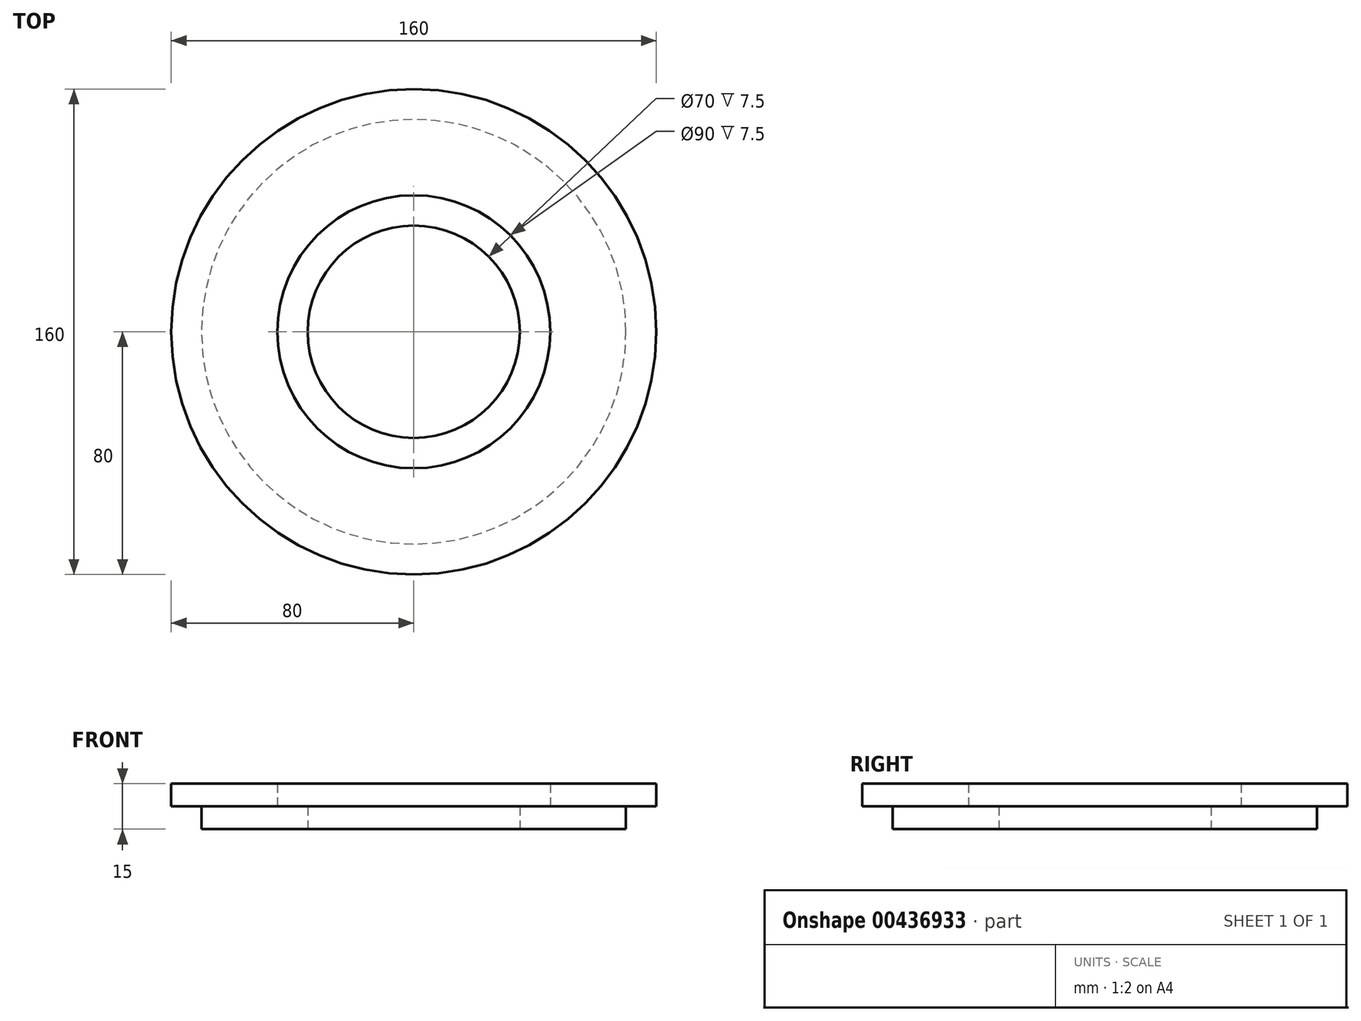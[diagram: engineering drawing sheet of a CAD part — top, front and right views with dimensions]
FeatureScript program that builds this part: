
annotation { "Feature Type Name" : "Feature", "Feature Type Description" : "" }
export const myFeature = defineFeature(function(context is Context, id is Id, definition is map)
    precondition{}
    {
        {
            var Q0;
            Q0=qCreatedBy(makeId("Front.planeOp"),FACE);
            var sketch = newSketch(context, id + "F0", { "sketchPlane" : qUnion([Q0])});
            skLineSegment(sketch, "E0", {"start": v(35, 0) * mm, "end": v(70, 0) * mm});
            skLineSegment(sketch, "E1", {"start": v(70, 0) * mm, "end": v(70, 7.5) * mm});
            skLineSegment(sketch, "E2", {"start": v(70, 7.5) * mm, "end": v(80, 7.5) * mm});
            skLineSegment(sketch, "E3", {"start": v(80, 7.5) * mm, "end": v(80, 15) * mm});
            skLineSegment(sketch, "E4", {"start": v(80, 15) * mm, "end": v(45, 15) * mm});
            skLineSegment(sketch, "E5", {"start": v(45, 15) * mm, "end": v(45, 7.5) * mm});
            skLineSegment(sketch, "E6", {"start": v(45, 7.5) * mm, "end": v(35, 7.5) * mm});
            skLineSegment(sketch, "E7", {"start": v(35, 7.5) * mm, "end": v(35, 0) * mm});
            skLineSegment(sketch, "E8", {"start": v(0, 0) * mm, "end": v(0, 115.63) * mm, "construction": true});
            skSolve(sketch);
        }
        {
            var Q0;
            Q0=makeQuery(id+"F0.imprint","IMPRINT",FACE,{"disambiguationData":[TD([[makeQuery(id+"F0.imprint","IMPRINT",EDGE,{"derivedFrom":sQuery(id+"F0.wireOp",EDGE,"E0")}),1.0]])]});
            var Q1;
            Q1=sQuery(id+"F0.wireOp",EDGE,"E8");
            var Q2;
            Q2=sQuery(id+"F0.wireOp",EDGE,"E8");
            revolve(context, id + "F1", {"entities" : qUnion([Q0]), "surfaceEntities" : qUnion([Q1]), "axis" : qUnion([Q2]), "revolveType" : RevolveType.FULL});
        }
    });
